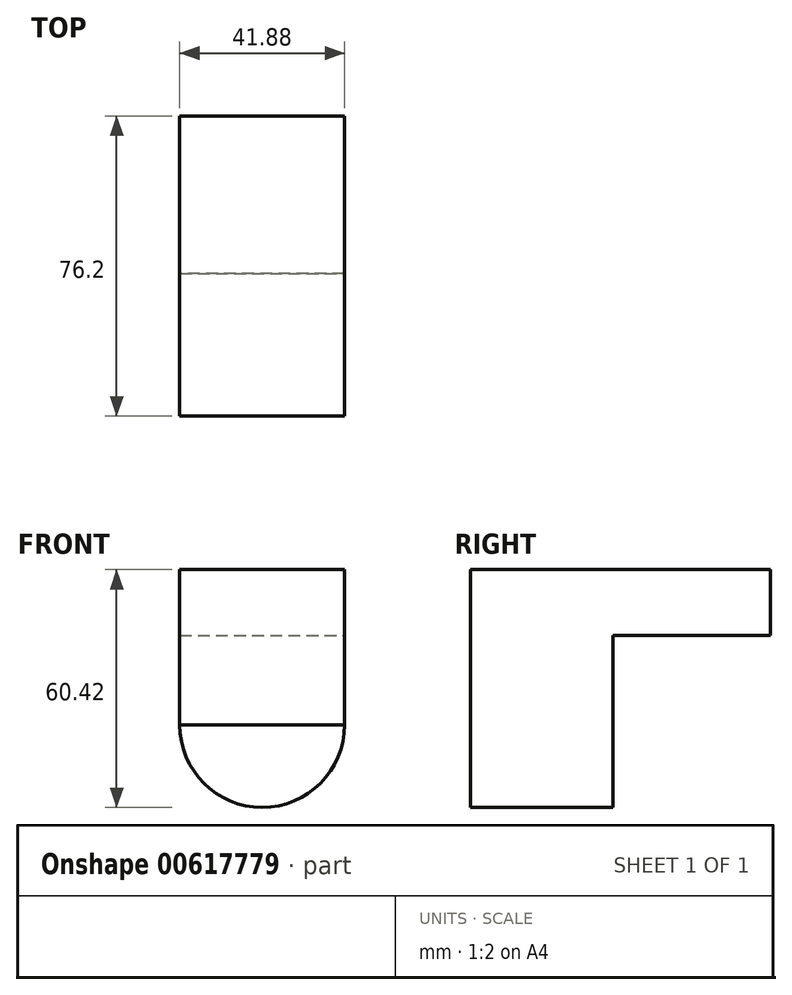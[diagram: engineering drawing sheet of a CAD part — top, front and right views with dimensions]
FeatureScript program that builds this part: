
annotation { "Feature Type Name" : "Feature", "Feature Type Description" : "" }
export const myFeature = defineFeature(function(context is Context, id is Id, definition is map)
    precondition{}
    {
        {
            var Q0;
            Q0=qCreatedBy(makeId("Front.planeOp"),FACE);
            var sketch = newSketch(context, id + "F0", { "sketchPlane" : qUnion([Q0])});
            skLineSegment(sketch, "E0", {"start": v(-49.63, 61.35) * mm, "end": v(-7.75, 61.35) * mm});
            skLineSegment(sketch, "E1", {"start": v(-49.63, 61.35) * mm, "end": v(-49.63, 21.87) * mm});
            skLineSegment(sketch, "E2", {"start": v(-49.63, 21.87) * mm, "end": v(-7.75, 21.87) * mm});
            skLineSegment(sketch, "E3", {"start": v(-7.75, 21.87) * mm, "end": v(-7.75, 61.35) * mm});
            skSolve(sketch);
        }
        {
            var Q0;
            Q0 = qSketchRegion(id + "F0", true);
            extrude(context, id + "F1", {"entities" : qUnion([Q0]), "depth" : 76.2 * mm, "offsetDistance" : 25.4 * mm});
        }
        {
            var Q0;
            Q0=makeQuery(id+"F1.opExtrude","SWEPT_FACE",FACE,{"disambiguationData":[OSD([sQuery(id+"F0.wireOp",EDGE,"E3")])]});
            var sketch = newSketch(context, id + "F2", { "sketchPlane" : qUnion([Q0])});
            skLineSegment(sketch, "E4", {"start": v(-39.98, 44.63) * mm, "end": v(-39.98, 21.87) * mm});
            skPoint(sketch, "E4.endSnap0", {"position": v(-38.1, 21.87) * mm});
            skLineSegment(sketch, "E5", {"start": v(-39.98, 21.87) * mm, "end": v(0, 21.87) * mm});
            skLineSegment(sketch, "E6", {"start": v(0, 21.87) * mm, "end": v(-39.98, 44.63) * mm});
            skSolve(sketch);
        }
        {
            var Q0;
            Q0 = qSketchRegion(id + "F2", true);
            extrude(context, id + "F3", {"entities" : qUnion([Q0]), "operationType" : NewBodyOperationType.REMOVE, "oppositeDirection" : true, "depth" : 76.2 * mm, "offsetDistance" : 25.4 * mm});
        }
        {
            var Q0;
            Q0=makeQuery(id+"F3.boolean.opBoolean","COPY",FACE,{"derivedFrom":makeQuery(id+"F3.opExtrude","SWEPT_FACE",FACE,{"disambiguationData":[OSD([sQuery(id+"F2.wireOp",EDGE,"E4")])]})});
            var sketch = newSketch(context, id + "F4", { "sketchPlane" : qUnion([Q0])});
            skArc(sketch, "E7", {"start": v(7.75, 21.87) * mm, "mid": v(28.69, 0.93) * mm, "end": v(49.63, 21.87) * mm});
            skSolve(sketch);
        }
        {
            var Q0;
            Q0=makeQuery(id+"F4.imprint","IMPRINT",FACE,{"disambiguationData":[TD([[makeQuery(id+"F4.imprint","IMPRINT",EDGE,{"derivedFrom":sQuery(id+"F4.wireOp",EDGE,"E7")}),1.0]])]});
            extrude(context, id + "F5", {"entities" : qUnion([Q0]), "operationType" : NewBodyOperationType.ADD, "oppositeDirection" : true, "depth" : 36.2 * mm, "offsetDistance" : 25.4 * mm});
        }
        {
            var Q0;
            Q0=makeQuery(id+"F1.opExtrude","SWEPT_FACE",FACE,{"disambiguationData":[OSD([sQuery(id+"F0.wireOp",EDGE,"E3")])]});
            var sketch = newSketch(context, id + "F6", { "sketchPlane" : qUnion([Q0])});
            skLineSegment(sketch, "E8", {"start": v(-39.98, 44.63) * mm, "end": v(0, 44.63) * mm});
            skSolve(sketch);
        }
        {
            var Q0;
            Q0 = qSketchRegion(id + "F6", true);
            var Q1;
            {var subQ0=sQuery(id+"F6.wireOp",EDGE,"E8");Q1=makeQuery(id+"F6.imprint","IMPRINT",FACE,{"disambiguationData":[TD([[makeQuery(id+"F6.imprint","IMPRINT",EDGE,{"derivedFrom":subQ0}),-1.0]])]});}
            extrude(context, id + "F7", {"entities" : qUnion([Q0, Q1]), "operationType" : NewBodyOperationType.REMOVE, "oppositeDirection" : true, "depth" : 76.2 * mm, "offsetDistance" : 25.4 * mm});
        }
    });
